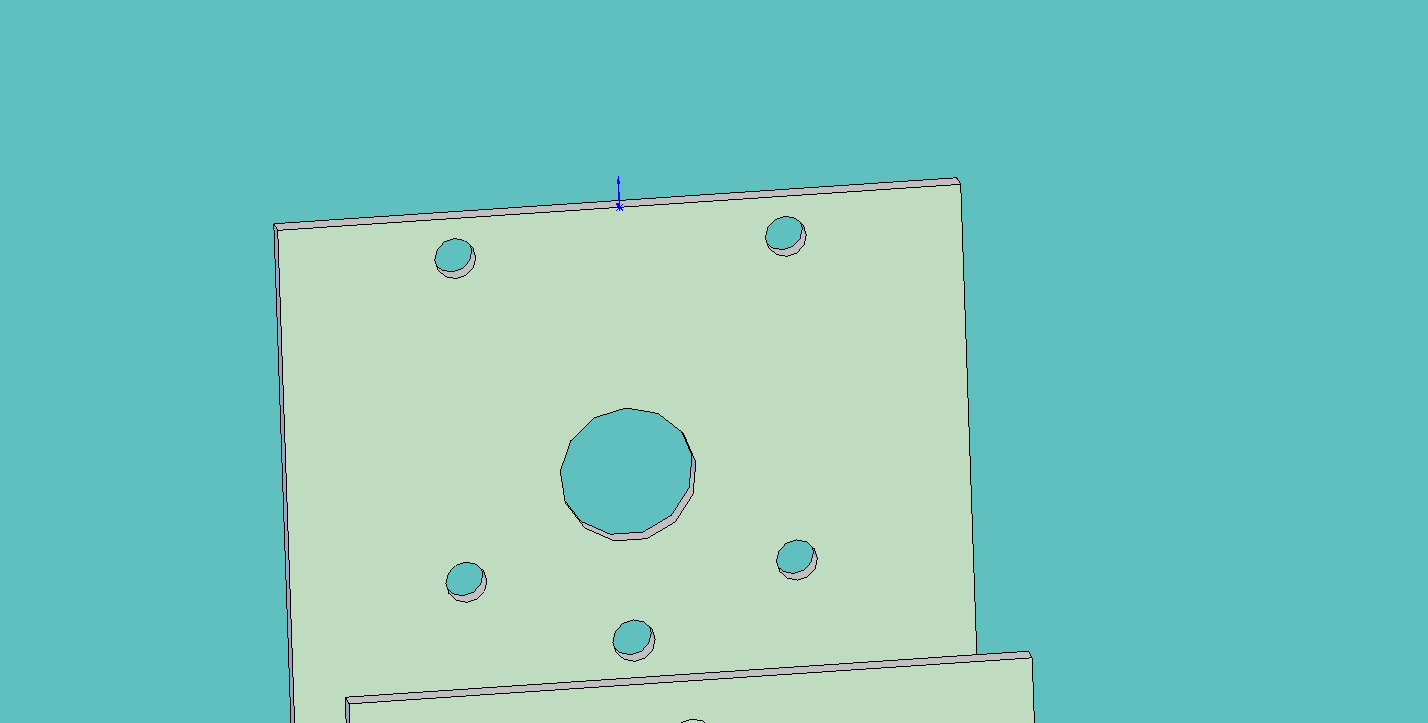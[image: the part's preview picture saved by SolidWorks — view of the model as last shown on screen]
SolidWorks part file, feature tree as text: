
SOLIDWORKS PART (.sldprt)
format: sldprt  version: not decoded by parser v0  size: 166,912 bytes
history: native  units: mm
features: sketch x4, plane x3, cut_extrude x3, material x1, extrude x1 (+8 scaffold rows collapsed)
feature tree (20):
  scaffold x8  (default folders/planes/origin — collapsed)
  material  "Matériau <non spécifié>"
  plane  "Plan de face"
  plane  "Plan de dessus"
  plane  "Plan de droite"
  sketch  "Esquisse1"  dims[D1=50.0mm D2=2.0mm D3=22.0mm D4=30.0mm]
  extrude  "Extrusion1"  Depth=50mm
  sketch  "Esquisse2"  dims[c1.D1=3.0mm c1.D2=10.0mm c1.D7=10.0mm c1.D3=3.0mm c1.D4=24.2mm c1.D5=12.1mm c1.D6=24.2mm c2.D7=7.2mm]
  cut_extrude  "Enlèv. mat.-Extru.1"  Depth=10mm
  sketch  "Esquisse3"  dims[c1.D2=3.1mm c1.D3=3.1mm c1.D1=17.6mm c2.D3=11.0mm]
  cut_extrude  "Enlèv. mat.-Extru.2"  [1 undecoded]
  sketch  "Esquisse4"  dims[c1.D1=~5.230336mm c1.D2=5.2mm c2.D1=20.0mm c2.D3=9.0mm c2.D4=40.0mm]
  cut_extrude  "Enlèv. mat.-Extru.3"  Depth=10mm
decode coverage: 7 of 8 modeling features carry decoded parameters
note: ~ marks probable driven/reference dimensions
note: 1 parameter value undecoded
note: suppression state not decoded; provenance and decode notes live in map.json
